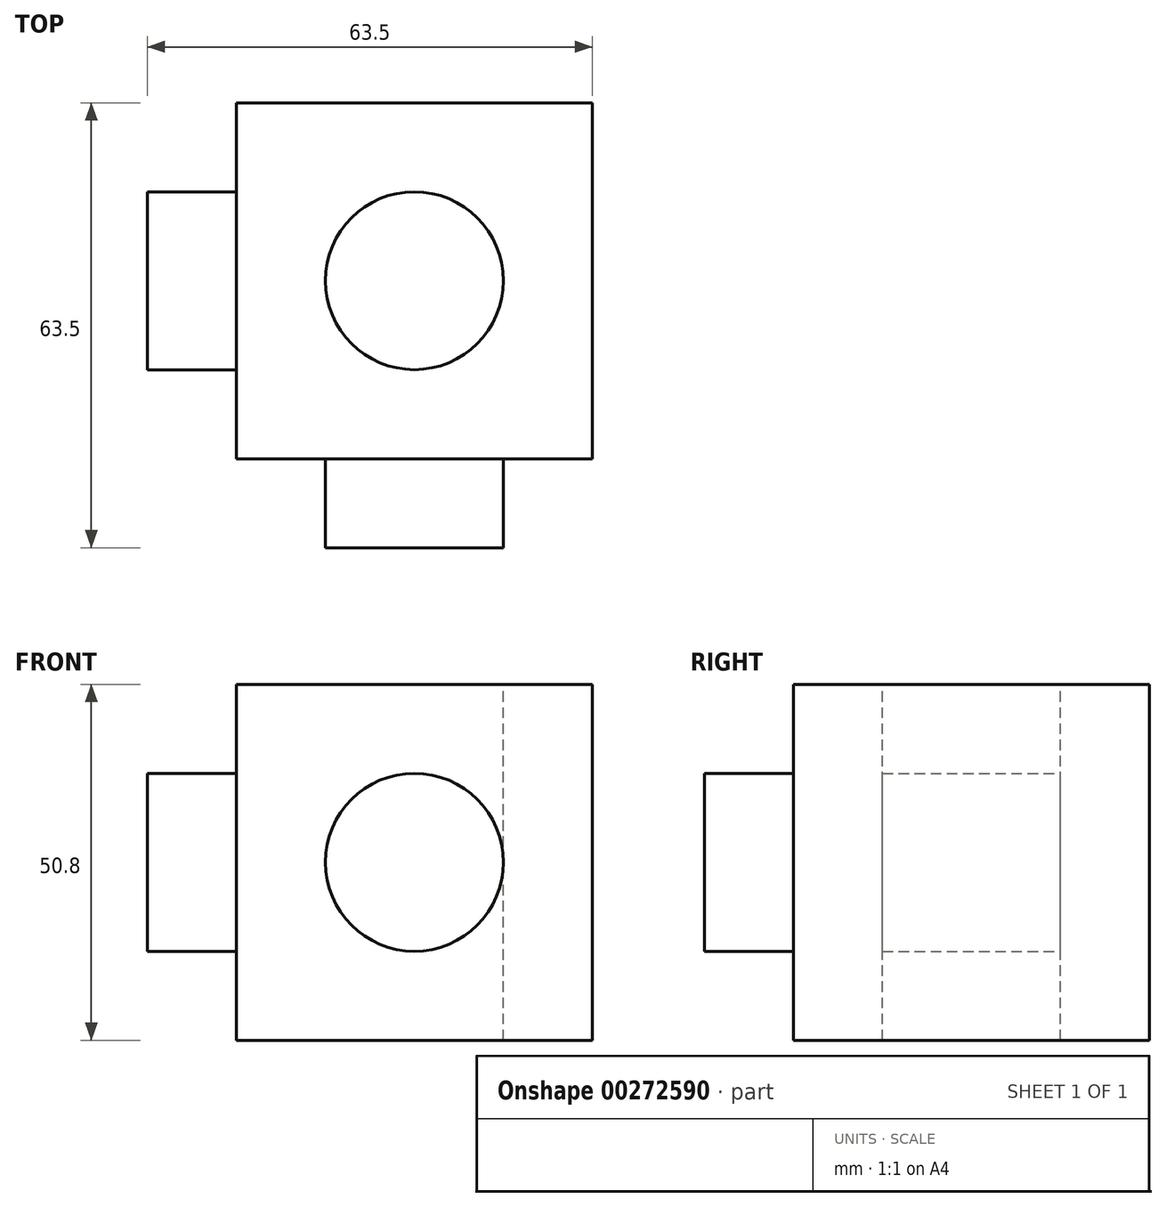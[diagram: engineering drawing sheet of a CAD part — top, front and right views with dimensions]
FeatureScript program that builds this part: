
annotation { "Feature Type Name" : "Feature", "Feature Type Description" : "" }
export const myFeature = defineFeature(function(context is Context, id is Id, definition is map)
    precondition{}
    {
        {
            var Q0;
            Q0=qCreatedBy(makeId("Front.planeOp"),FACE);
            var sketch = newSketch(context, id + "F0", { "sketchPlane" : qUnion([Q0])});
            skLineSegment(sketch, "E0.bottom", {"start": v(0, 0) * mm, "end": v(-50.8, 0) * mm});
            skLineSegment(sketch, "E0.top", {"start": v(0, 50.8) * mm, "end": v(-50.8, 50.8) * mm});
            skLineSegment(sketch, "E0.left", {"start": v(0, 0) * mm, "end": v(0, 50.8) * mm});
            skLineSegment(sketch, "E0.right", {"start": v(-50.8, 0) * mm, "end": v(-50.8, 50.8) * mm});
            skSolve(sketch);
        }
        {
            var Q0;
            Q0 = qSketchRegion(id + "F0", true);
            extrude(context, id + "F1", {"entities" : qUnion([Q0]), "depth" : 50.8 * mm});
        }
        {
            var Q0;
            Q0=makeQuery(id+"F1.opExtrude","SWEPT_FACE",FACE,{"disambiguationData":[OSD([sQuery(id+"F0.wireOp",EDGE,"E0.top")])]});
            var sketch = newSketch(context, id + "F2", { "sketchPlane" : qUnion([Q0])});
            skCircle(sketch, "E1", {"center": v(-25.4, -25.4) * mm, "radius": 12.7 * mm});
            skSolve(sketch);
        }
        {
            var Q0;
            Q0 = qSketchRegion(id + "F2", true);
            extrude(context, id + "F3", {"entities" : qUnion([Q0]), "operationType" : NewBodyOperationType.REMOVE, "oppositeDirection" : true, "depth" : 50.8 * mm});
        }
        {
            var Q0;
            Q0=makeQuery(id+"F1.opExtrude","SWEPT_FACE",FACE,{"disambiguationData":[OSD([sQuery(id+"F0.wireOp",EDGE,"E0.right")])]});
            var sketch = newSketch(context, id + "F4", { "sketchPlane" : qUnion([Q0])});
            skLineSegment(sketch, "E2.bottom", {"start": v(38.1, 12.7) * mm, "end": v(12.7, 12.7) * mm});
            skLineSegment(sketch, "E2.top", {"start": v(38.1, 38.1) * mm, "end": v(12.7, 38.1) * mm});
            skLineSegment(sketch, "E2.left", {"start": v(38.1, 12.7) * mm, "end": v(38.1, 38.1) * mm});
            skLineSegment(sketch, "E2.right", {"start": v(12.7, 12.7) * mm, "end": v(12.7, 38.1) * mm});
            skSolve(sketch);
        }
        {
            var Q0;
            Q0 = qSketchRegion(id + "F4", true);
            extrude(context, id + "F5", {"entities" : qUnion([Q0]), "operationType" : NewBodyOperationType.ADD, "depth" : 12.7 * mm});
        }
        {
            var Q0;
            Q0=makeQuery(id+"F1.opExtrude","CAP_FACE",FACE,{"disambiguationData":[OSD([sQuery(id+"F0.wireOp",EDGE,"E0.bottom"),sQuery(id+"F0.wireOp",EDGE,"E0.top"),sQuery(id+"F0.wireOp",EDGE,"E0.left"),sQuery(id+"F0.wireOp",EDGE,"E0.right")])],"isStart":false});
            var sketch = newSketch(context, id + "F6", { "sketchPlane" : qUnion([Q0])});
            skCircle(sketch, "E3", {"center": v(-25.4, 25.4) * mm, "radius": 12.7 * mm});
            skSolve(sketch);
        }
        {
            var Q0;
            Q0=makeQuery(id+"F6.imprint","IMPRINT",FACE,{"disambiguationData":[TD([[makeQuery(id+"F6.imprint","IMPRINT",EDGE,{"derivedFrom":sQuery(id+"F6.wireOp",EDGE,"E3")}),1.0]])]});
            extrude(context, id + "F7", {"entities" : qUnion([Q0]), "operationType" : NewBodyOperationType.ADD, "depth" : 12.7 * mm});
        }
    });
